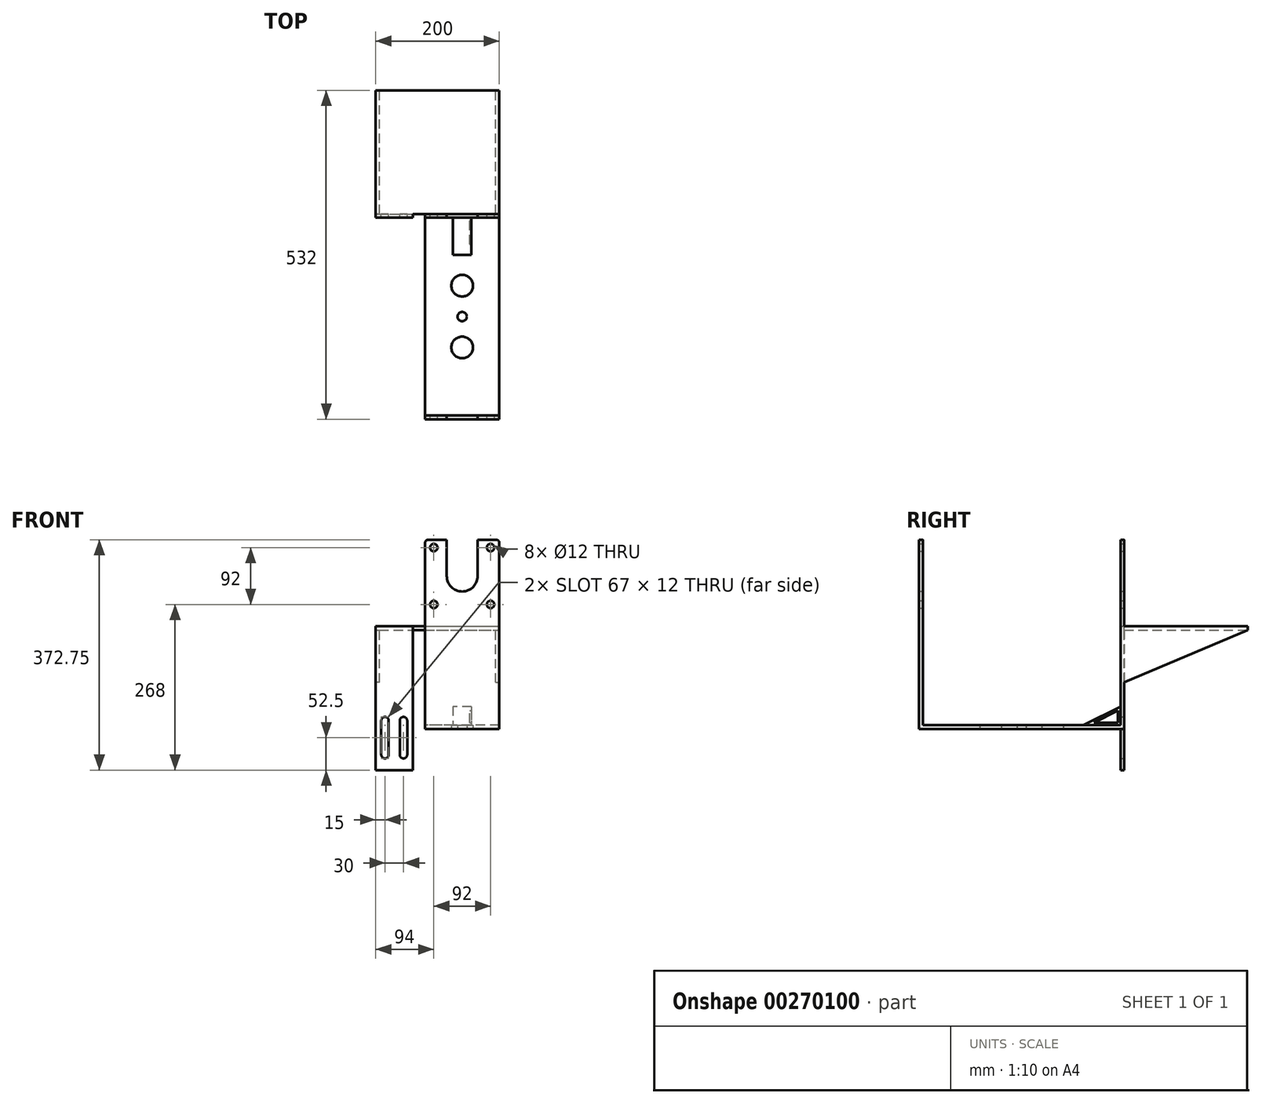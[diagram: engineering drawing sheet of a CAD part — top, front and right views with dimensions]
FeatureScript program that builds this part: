
annotation { "Feature Type Name" : "Feature", "Feature Type Description" : "" }
export const myFeature = defineFeature(function(context is Context, id is Id, definition is map)
    precondition{}
    {
        {
            var Q0;
            Q0=qCreatedBy(makeId("Right.planeOp"),FACE);
            var sketch = newSketch(context, id + "F0", { "sketchPlane" : qUnion([Q0])});
            skLineSegment(sketch, "E0", {"start": v(-160, 150) * mm, "end": v(-160, -150) * mm});
            skLineSegment(sketch, "E1", {"start": v(-160, -150) * mm, "end": v(160, -150) * mm});
            skLineSegment(sketch, "E2", {"start": v(160, -150) * mm, "end": v(160, 150) * mm});
            skPoint(sketch, "E3", {"position": v(-160, 0) * mm});
            skPoint(sketch, "E4", {"position": v(0, -150) * mm});
            skSolve(sketch);
        }
        {
            var Q0;
            Q0=qCreatedBy(makeId("Top.planeOp"),FACE);
            cPlane(context, id + "F1", {"entities" : qUnion([Q0]), "cplaneType" : CPlaneType.OFFSET, "offset" : 150 * mm, "width" : 150 * mm, "height" : 150 * mm});
        }
        {
            var Q0;
            Q0=qCreatedBy(id+"F1.planeOp",FACE);
            var sketch = newSketch(context, id + "F2", { "sketchPlane" : qUnion([Q0])});
            skLineSegment(sketch, "E5.bottom", {"start": v(-60, -160) * mm, "end": v(60, -160) * mm});
            skLineSegment(sketch, "E5.top", {"start": v(-60, -166) * mm, "end": v(60, -166) * mm});
            skLineSegment(sketch, "E5.left", {"start": v(-60, -160) * mm, "end": v(-60, -166) * mm});
            skLineSegment(sketch, "E5.right", {"start": v(60, -160) * mm, "end": v(60, -166) * mm});
            skPoint(sketch, "E6", {"position": v(0, -160) * mm});
            skSolve(sketch);
        }
        {
            var Q0;
            Q0=makeQuery(id+"F2.imprint","IMPRINT",FACE,{"disambiguationData":[TD([[makeQuery(id+"F2.imprint","IMPRINT",EDGE,{"derivedFrom":sQuery(id+"F2.wireOp",EDGE,"E5.bottom")}),-1.0]])]});
            var Q1;
            Q1=sQuery(id+"F0.wireOp",EDGE,"E0");
            var Q2;
            Q2=sQuery(id+"F0.wireOp",EDGE,"E1");
            var Q3;
            Q3=sQuery(id+"F0.wireOp",EDGE,"E2");
            sweep(context, id + "F3", {"profiles" : qUnion([Q0]), "path" : qUnion([Q1, Q2, Q3])});
        }
        {
            var Q0;
            Q0=makeQuery(id+"F3.opSweep","SWEPT_FACE",FACE,{"disambiguationData":[OSD([sQuery(id+"F0.wireOp",EDGE,"E0"),sQuery(id+"F2.wireOp",EDGE,"E5.top")])]});
            var sketch = newSketch(context, id + "F4", { "sketchPlane" : qUnion([Q0])});
            skPoint(sketch, "E7", {"position": v(-46, 137.25) * mm});
            skPoint(sketch, "E8", {"position": v(46, 137.25) * mm});
            skPoint(sketch, "E9", {"position": v(46, 45.25) * mm});
            skPoint(sketch, "E10", {"position": v(-46, 45.25) * mm});
            skLineSegment(sketch, "E11", {"start": v(0, 144.43) * mm, "end": v(0, -38.98) * mm, "construction": true});
            skPoint(sketch, "E11.endSnap0", {"position": v(0, 150) * mm});
            skSolve(sketch);
        }
        {
            var Q0;
            Q0=sQuery(id+"F4.wireOp",VERTEX,"E7");
            var Q1;
            Q1=sQuery(id+"F4.wireOp",VERTEX,"E10");
            var Q2;
            Q2=sQuery(id+"F4.wireOp",VERTEX,"E9");
            var Q3;
            Q3=sQuery(id+"F4.wireOp",VERTEX,"E8");
            var Q4;
            Q4=makeQuery(id+"F3.opSweep","SWEPT_BODY",BODY,{"disambiguationData":[OSD([sQuery(id+"F0.wireOp",EDGE,"E2"),sQuery(id+"F2.wireOp",EDGE,"E5.bottom"),sQuery(id+"F2.wireOp",EDGE,"E5.top"),sQuery(id+"F2.wireOp",EDGE,"E5.left"),sQuery(id+"F2.wireOp",EDGE,"E5.right")])]});
            hole(context, id + "F5", {"style" : HoleStyle.SIMPLE, "endStyle" : HoleEndStyle.THROUGH, "standardTappedOrClearance" : lookupTablePath({ "standard" : "ISO", "size" : "12", "type" : "Drilled" }), "standardBlindInLast" : lookupTablePath({ "standard" : "ISO", "size" : "12", "type" : "Drilled" }), "holeDiameter" : 12 * mm, "tappedDepth" : 12 * mm, "tapClearance" : 3, "startFromSketch" : true, "locations" : qUnion([Q0, Q1, Q2, Q3]), "scope" : qUnion([Q4])});
        }
        {
            var Q0;
            Q0=makeQuery(id+"F3.opSweep","SWEPT_FACE",FACE,{"disambiguationData":[OSD([sQuery(id+"F0.wireOp",EDGE,"E0"),sQuery(id+"F2.wireOp",EDGE,"E5.top")])]});
            var sketch = newSketch(context, id + "F6", { "sketchPlane" : qUnion([Q0])});
            skLineSegment(sketch, "E12.bottom", {"start": v(-25, 150) * mm, "end": v(25, 150) * mm});
            skLineSegment(sketch, "E12.left", {"start": v(-25, 150) * mm, "end": v(-25, 91.25) * mm});
            skLineSegment(sketch, "E12.right", {"start": v(25, 150) * mm, "end": v(25, 91.25) * mm});
            skCircle(sketch, "E13.0", {"center": v(46, 45.25) * mm, "radius": 6 * mm});
            skCircle(sketch, "E13.1", {"center": v(46, 137.25) * mm, "radius": 6 * mm});
            skCircle(sketch, "E13.2", {"center": v(-46, 137.25) * mm, "radius": 6 * mm});
            skCircle(sketch, "E13.3", {"center": v(-46, 45.25) * mm, "radius": 6 * mm});
            skArc(sketch, "E14", {"start": v(-25, 91.25) * mm, "mid": v(0, 66.25) * mm, "end": v(25, 91.25) * mm});
            skCircle(sketch, "E15", {"center": v(0, 91.25) * mm, "radius": 15 * mm, "construction": true});
            skSolve(sketch);
        }
        {
            var Q0;
            Q0=makeQuery(id+"F6.imprint","IMPRINT",FACE,{"disambiguationData":[TD([[makeQuery(id+"F6.imprint","IMPRINT",EDGE,{"derivedFrom":sQuery(id+"F6.wireOp",EDGE,"E12.bottom")}),1.0]])]});
            var Q1;
            Q1=makeQuery(id+"F3.opSweep","SWEPT_FACE",FACE,{"disambiguationData":[OSD([sQuery(id+"F0.wireOp",EDGE,"E2"),sQuery(id+"F2.wireOp",EDGE,"E5.top")])]});
            extrude(context, id + "F7", {"entities" : qUnion([Q0]), "operationType" : NewBodyOperationType.REMOVE, "endBound" : BoundingType.UP_TO_SURFACE, "oppositeDirection" : true, "endBoundEntityFace" : qUnion([Q1]), "depth" : 25 * mm});
        }
        {
            var Q0;
            Q0=qCreatedBy(makeId("Right.planeOp"),FACE);
            var sketch = newSketch(context, id + "F8", { "sketchPlane" : qUnion([Q0])});
            skLineSegment(sketch, "E16", {"start": v(160, -120) * mm, "end": v(100, -150) * mm});
            skLineSegment(sketch, "E17", {"start": v(100, -150) * mm, "end": v(160, -150) * mm});
            skLineSegment(sketch, "E18", {"start": v(160, -120) * mm, "end": v(160, -150) * mm});
            skSolve(sketch);
        }
        {
            var Q0;
            Q0=makeQuery(id+"F8.imprint","IMPRINT",FACE,{"disambiguationData":[TD([[makeQuery(id+"F8.imprint","IMPRINT",EDGE,{"derivedFrom":sQuery(id+"F8.wireOp",EDGE,"E16")}),1.0]])]});
            extrude(context, id + "F9", {"entities" : qUnion([Q0]), "operationType" : NewBodyOperationType.ADD, "depth" : 30 * mm, "symmetric" : true});
        }
        {
            var Q0;
            Q0=makeQuery(id+"F9.opExtrude","CAP_FACE",FACE,{"disambiguationData":[OSD([sQuery(id+"F8.wireOp",EDGE,"E16"),sQuery(id+"F8.wireOp",EDGE,"E17"),sQuery(id+"F8.wireOp",EDGE,"E18")])],"isStart":false});
            var sketch = newSketch(context, id + "F10", { "sketchPlane" : qUnion([Q0])});
            skLineSegment(sketch, "E19.0", {"start": v(156, -146) * mm, "end": v(156, -126.47) * mm});
            skLineSegment(sketch, "E19.1", {"start": v(116.94, -146) * mm, "end": v(156, -146) * mm});
            skLineSegment(sketch, "E19.2", {"start": v(156, -126.47) * mm, "end": v(116.94, -146) * mm});
            skSolve(sketch);
        }
        {
            var Q0;
            Q0=makeQuery(id+"F10.imprint","IMPRINT",FACE,{"disambiguationData":[TD([[makeQuery(id+"F10.imprint","IMPRINT",EDGE,{"derivedFrom":sQuery(id+"F10.wireOp",EDGE,"E19.0")}),1.0]])]});
            extrude(context, id + "F11", {"entities" : qUnion([Q0]), "operationType" : NewBodyOperationType.REMOVE, "oppositeDirection" : true, "depth" : 3 * mm});
        }
        {
            var Q0;
            Q0=makeQuery(id+"F3.opSweep","CAP_EDGE",EDGE,{"disambiguationData":[OSD([sQuery(id+"F0.wireOp",VERTEX,"E0.start"),sQuery(id+"F2.wireOp",EDGE,"E5.right")])],"isStart":true});
            var Q1;
            Q1=makeQuery(id+"F3.opSweep","CAP_EDGE",EDGE,{"disambiguationData":[OSD([sQuery(id+"F0.wireOp",VERTEX,"E0.start"),sQuery(id+"F2.wireOp",EDGE,"E5.left")])],"isStart":true});
            var Q2;
            Q2=makeQuery(id+"F3.opSweep","CAP_EDGE",EDGE,{"disambiguationData":[OSD([sQuery(id+"F0.wireOp",VERTEX,"E2.end"),sQuery(id+"F2.wireOp",EDGE,"E5.left")])],"isStart":false});
            var Q3;
            Q3=makeQuery(id+"F3.opSweep","CAP_EDGE",EDGE,{"disambiguationData":[OSD([sQuery(id+"F0.wireOp",VERTEX,"E2.end"),sQuery(id+"F2.wireOp",EDGE,"E5.right")])],"isStart":false});
            fillet(context, id + "F12", {"entities" : qUnion([Q0, Q1, Q2, Q3]), "radius" : 5 * mm, "tangentPropagation" : true, "allowEdgeOverflow" : false});
        }
        {
            var Q0;
            Q0=makeQuery(id+"F3.opSweep","SWEPT_FACE",FACE,{"disambiguationData":[OSD([sQuery(id+"F0.wireOp",EDGE,"E1"),sQuery(id+"F2.wireOp",EDGE,"E5.bottom")])]});
            var sketch = newSketch(context, id + "F13", { "sketchPlane" : qUnion([Q0])});
            skPoint(sketch, "E20", {"position": v(0, -50) * mm});
            skPoint(sketch, "E21", {"position": v(0, 50) * mm});
            skPoint(sketch, "E22", {"position": v(0, 0) * mm});
            skSolve(sketch);
        }
        {
            var Q0;
            Q0=sQuery(id+"F13.wireOp",VERTEX,"E21");
            var Q1;
            Q1=sQuery(id+"F13.wireOp",VERTEX,"E20");
            var Q2;
            Q2=makeQuery(id+"F3.opSweep","SWEPT_BODY",BODY,{"disambiguationData":[OSD([sQuery(id+"F0.wireOp",EDGE,"E2"),sQuery(id+"F2.wireOp",EDGE,"E5.bottom"),sQuery(id+"F2.wireOp",EDGE,"E5.top"),sQuery(id+"F2.wireOp",EDGE,"E5.left"),sQuery(id+"F2.wireOp",EDGE,"E5.right")])]});
            hole(context, id + "F14", {"style" : HoleStyle.SIMPLE, "endStyle" : HoleEndStyle.THROUGH, "holeDiameter" : 35 * mm, "tappedDepth" : 12 * mm, "tapClearance" : 3, "startFromSketch" : true, "locations" : qUnion([Q0, Q1]), "scope" : qUnion([Q2])});
        }
        {
            var Q0;
            Q0=sQuery(id+"F13.wireOp",VERTEX,"E22");
            var Q1;
            Q1=makeQuery(id+"F3.opSweep","SWEPT_BODY",BODY,{"disambiguationData":[OSD([sQuery(id+"F0.wireOp",EDGE,"E2"),sQuery(id+"F2.wireOp",EDGE,"E5.bottom"),sQuery(id+"F2.wireOp",EDGE,"E5.top"),sQuery(id+"F2.wireOp",EDGE,"E5.left"),sQuery(id+"F2.wireOp",EDGE,"E5.right")])]});
            hole(context, id + "F15", {"style" : HoleStyle.SIMPLE, "endStyle" : HoleEndStyle.THROUGH, "holeDiameter" : 15 * mm, "tappedDepth" : 12 * mm, "tapClearance" : 3, "startFromSketch" : true, "locations" : qUnion([Q0]), "scope" : qUnion([Q1])});
        }
        {
            var Q0;
            Q0=makeQuery(id+"F3.opSweep","SWEPT_FACE",FACE,{"disambiguationData":[OSD([sQuery(id+"F0.wireOp",EDGE,"E0"),sQuery(id+"F2.wireOp",EDGE,"E5.right")])]});
            var sketch = newSketch(context, id + "F16", { "sketchPlane" : qUnion([Q0])});
            skLineSegment(sketch, "E23.bottom", {"start": v(166, 10) * mm, "end": v(366, 10) * mm});
            skLineSegment(sketch, "E23.top", {"start": v(166, 4) * mm, "end": v(366, 4) * mm});
            skLineSegment(sketch, "E23.left", {"start": v(166, 10) * mm, "end": v(166, 4) * mm});
            skLineSegment(sketch, "E23.right", {"start": v(366, 10) * mm, "end": v(366, 4) * mm});
            skLineSegment(sketch, "E24", {"start": v(366, 4) * mm, "end": v(166, -81) * mm});
            skSolve(sketch);
        }
        {
            var Q0;
            Q0=makeQuery(id+"F16.imprint","IMPRINT",FACE,{"disambiguationData":[TD([[makeQuery(id+"F16.imprint","IMPRINT",EDGE,{"derivedFrom":sQuery(id+"F16.wireOp",EDGE,"E23.bottom")}),-1.0]])]});
            extrude(context, id + "F17", {"entities" : qUnion([Q0]), "operationType" : NewBodyOperationType.ADD, "oppositeDirection" : true, "depth" : 200 * mm});
        }
        {
            var Q0;
            {var subQ0=sQuery(id+"F16.wireOp",EDGE,"E23.top");Q0=makeQuery(id+"F16.imprint","IMPRINT",FACE,{"disambiguationData":[TD([[makeQuery(id+"F16.imprint","IMPRINT",EDGE,{"derivedFrom":subQ0}),-1.0]])]});}
            extrude(context, id + "F18", {"entities" : qUnion([Q0]), "operationType" : NewBodyOperationType.ADD, "oppositeDirection" : true, "depth" : 6 * mm});
        }
        {
            var Q0;
            Q0=makeQuery(id+"F17.opExtrude","SWEPT_FACE",FACE,{"disambiguationData":[OSD([sQuery(id+"F16.wireOp",EDGE,"E23.left")])]});
            var sketch = newSketch(context, id + "F19", { "sketchPlane" : qUnion([Q0])});
            skLineSegment(sketch, "E25.bottom", {"start": v(-140, 10) * mm, "end": v(-80, 10) * mm});
            skLineSegment(sketch, "E25.top", {"start": v(-140, -222.75) * mm, "end": v(-80, -222.75) * mm});
            skLineSegment(sketch, "E25.left", {"start": v(-140, 10) * mm, "end": v(-140, -222.75) * mm});
            skLineSegment(sketch, "E25.right", {"start": v(-80, 10) * mm, "end": v(-80, -222.75) * mm});
            skArc(sketch, "E26", {"start": v(-119, -142.75) * mm, "mid": v(-125, -136.75) * mm, "end": v(-131, -142.75) * mm});
            skArc(sketch, "E27", {"start": v(-131, -197.75) * mm, "mid": v(-125, -203.75) * mm, "end": v(-119, -197.75) * mm});
            skLineSegment(sketch, "E28", {"start": v(-119, -142.75) * mm, "end": v(-119, -197.75) * mm});
            skLineSegment(sketch, "E29", {"start": v(-131, -142.75) * mm, "end": v(-131, -197.75) * mm});
            skLineSegment(sketch, "E30", {"start": v(-110, 32.4) * mm, "end": v(-110, -153.35) * mm, "construction": true});
            skArc(sketch, "E31.MirrorCS", {"start": v(-101, -142.75) * mm, "mid": v(-95, -136.75) * mm, "end": v(-89, -142.75) * mm});
            skLineSegment(sketch, "E32.MirrorCS", {"start": v(-101, -142.75) * mm, "end": v(-101, -197.75) * mm});
            skLineSegment(sketch, "E33.MirrorCS", {"start": v(-89, -142.75) * mm, "end": v(-89, -197.75) * mm});
            skArc(sketch, "E34.MirrorCS", {"start": v(-89, -197.75) * mm, "mid": v(-95, -203.75) * mm, "end": v(-101, -197.75) * mm});
            skSolve(sketch);
        }
        {
            var Q0;
            {var subQ0=sQuery(id+"F19.wireOp",EDGE,"E25.bottom");Q0=makeQuery(id+"F19.imprint","IMPRINT",FACE,{"disambiguationData":[TD([[makeQuery(id+"F19.imprint","IMPRINT",EDGE,{"derivedFrom":subQ0}),-1.0]])]});}
            var Q1;
            {var subQ0=sQuery(id+"F19.wireOp",EDGE,"E25.top");Q1=makeQuery(id+"F19.imprint","IMPRINT",FACE,{"disambiguationData":[TD([[makeQuery(id+"F19.imprint","IMPRINT",EDGE,{"derivedFrom":subQ0}),1.0]])]});}
            extrude(context, id + "F20", {"entities" : qUnion([Q0, Q1]), "operationType" : NewBodyOperationType.ADD, "depth" : 6 * mm});
        }
        {
            var Q0;
            Q0=makeQuery(id+"F20.boolean.opBoolean","MERGE",FACE,{"derivedFrom":[makeQuery(id+"F17.opExtrude","CAP_FACE",FACE,{"disambiguationData":[OSD([sQuery(id+"F16.wireOp",EDGE,"E23.bottom"),sQuery(id+"F16.wireOp",EDGE,"E23.top"),sQuery(id+"F16.wireOp",EDGE,"E23.left"),sQuery(id+"F16.wireOp",EDGE,"E23.right")])],"isStart":false}),makeQuery(id+"F20.opExtrude","SWEPT_FACE",FACE,{"disambiguationData":[OSD([sQuery(id+"F19.wireOp",EDGE,"E25.left")])]})]});
            var sketch = newSketch(context, id + "F21", { "sketchPlane" : qUnion([Q0])});
            skLineSegment(sketch, "E35", {"start": v(-166, 4) * mm, "end": v(-366, 4) * mm});
            skLineSegment(sketch, "E36", {"start": v(-366, 4) * mm, "end": v(-166, -81) * mm});
            skLineSegment(sketch, "E37", {"start": v(-166, -81) * mm, "end": v(-166, 4) * mm});
            skSolve(sketch);
        }
        {
            var Q0;
            Q0=makeQuery(id+"F21.imprint","IMPRINT",FACE,{"disambiguationData":[TD([[makeQuery(id+"F21.imprint","IMPRINT",EDGE,{"derivedFrom":sQuery(id+"F21.wireOp",EDGE,"E35")}),1.0]])]});
            extrude(context, id + "F22", {"entities" : qUnion([Q0]), "operationType" : NewBodyOperationType.ADD, "oppositeDirection" : true, "depth" : 6 * mm});
        }
    });
